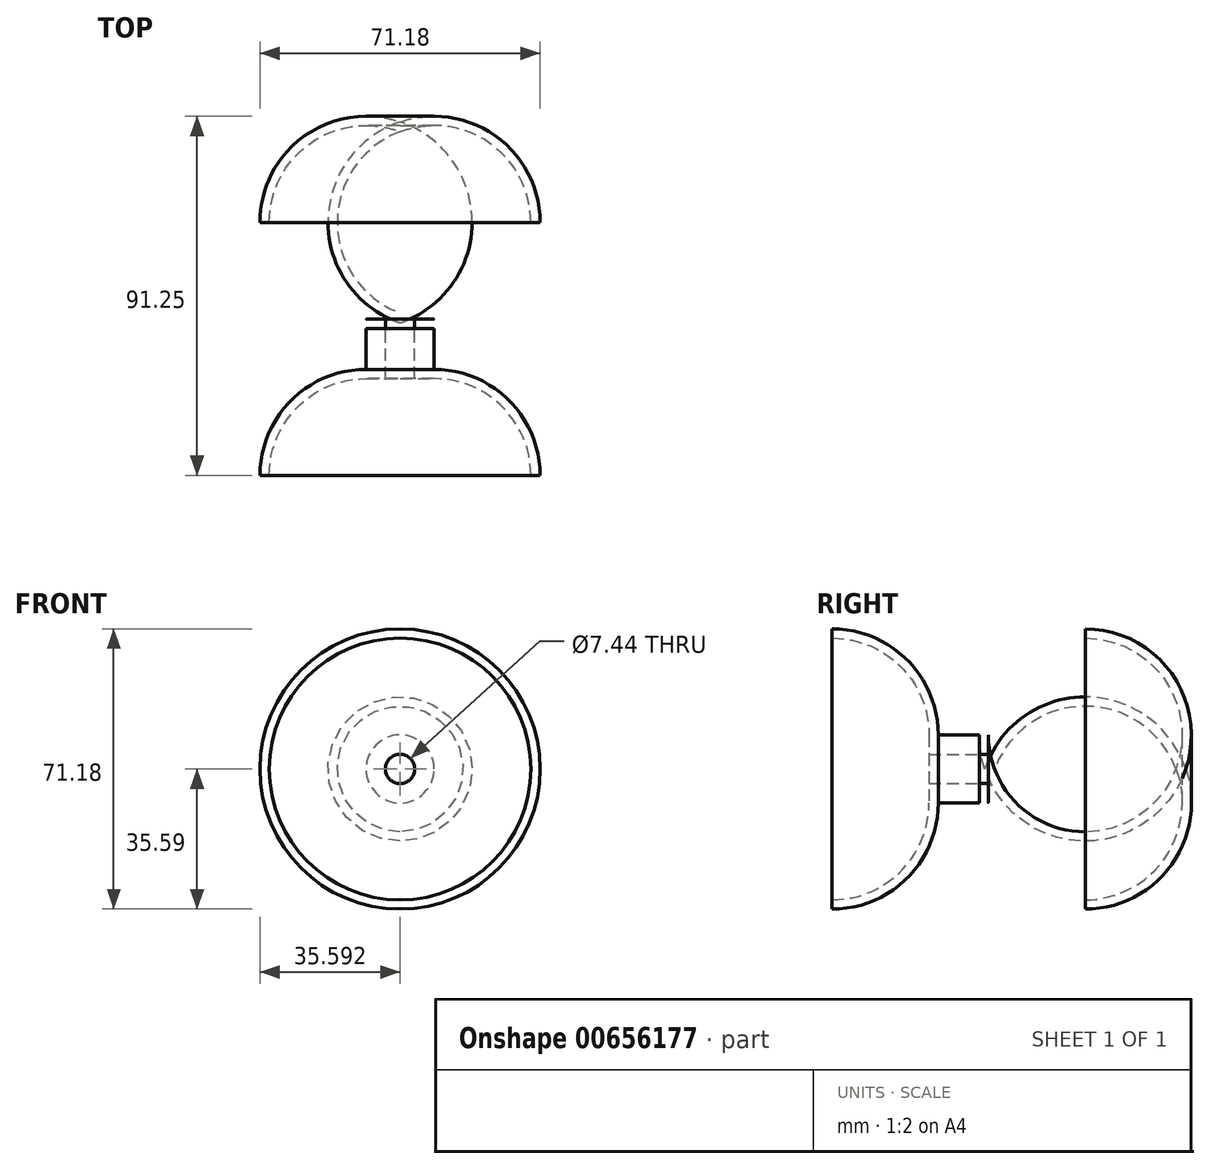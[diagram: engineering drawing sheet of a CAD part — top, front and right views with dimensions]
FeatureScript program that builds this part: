
annotation { "Feature Type Name" : "Feature", "Feature Type Description" : "" }
export const myFeature = defineFeature(function(context is Context, id is Id, definition is map)
    precondition{}
    {
        {
            var Q0;
            Q0=qCreatedBy(makeId("Top.planeOp"),FACE);
            var sketch = newSketch(context, id + "F0", { "sketchPlane" : qUnion([Q0])});
            skArc(sketch, "E0", {"start": v(-71.78, 45.83) * mm, "mid": v(-64.57, 28.42) * mm, "end": v(-47.17, 21.22) * mm});
            skArc(sketch, "E1", {"start": v(-74.13, 45.83) * mm, "mid": v(-66.23, 26.76) * mm, "end": v(-47.17, 18.87) * mm});
            skLineSegment(sketch, "E2", {"start": v(-71.78, 45.83) * mm, "end": v(-74.13, 45.83) * mm});
            skLineSegment(sketch, "E3", {"start": v(-38.54, 18.87) * mm, "end": v(-38.54, 0) * mm});
            skPoint(sketch, "E4.start.orphan", {"position": v(-38.54, 19.17) * mm});
            skLineSegment(sketch, "E5", {"start": v(-38.54, 18.87) * mm, "end": v(-38.54, 19.17) * mm});
            skLineSegment(sketch, "E6", {"start": v(-47.17, 13.68) * mm, "end": v(-77.23, 13.68) * mm});
            skLineSegment(sketch, "E7.MirrorCS", {"start": v(-71.78, -18.47) * mm, "end": v(-74.13, -18.47) * mm});
            skArc(sketch, "E8.MirrorCS", {"start": v(-74.13, -18.47) * mm, "mid": v(-66.23, 0.59) * mm, "end": v(-47.17, 8.48) * mm});
            skArc(sketch, "E9.MirrorCS", {"start": v(-71.78, -18.47) * mm, "mid": v(-64.57, -1.07) * mm, "end": v(-47.17, 6.14) * mm});
            skLineSegment(sketch, "E10", {"start": v(-47.17, 8.48) * mm, "end": v(-47.17, 18.87) * mm});
            skLineSegment(sketch, "E11", {"start": v(-47.17, 6.14) * mm, "end": v(-42.26, 6.14) * mm});
            skLineSegment(sketch, "E12", {"start": v(-42.26, 6.14) * mm, "end": v(-42.26, 21.22) * mm});
            skLineSegment(sketch, "E13", {"start": v(-42.26, 21.22) * mm, "end": v(-47.17, 21.22) * mm});
            skSolve(sketch);
        }
        {
            var Q0;
            {var subQ1=sQuery(id+"F0.wireOp",EDGE,"E0");Q0=makeQuery(id+"F0.imprint","IMPRINT",FACE,{"disambiguationData":[TD([[makeQuery(id+"F0.imprint","IMPRINT",EDGE,{"derivedFrom":subQ1}),-1.0]])]});}
            var Q1;
            Q1=sQuery(id+"F0.wireOp",EDGE,"E3");
            revolve(context, id + "F1", {"entities" : qUnion([Q0]), "axis" : qUnion([Q1]), "revolveType" : RevolveType.FULL});
        }
    });
